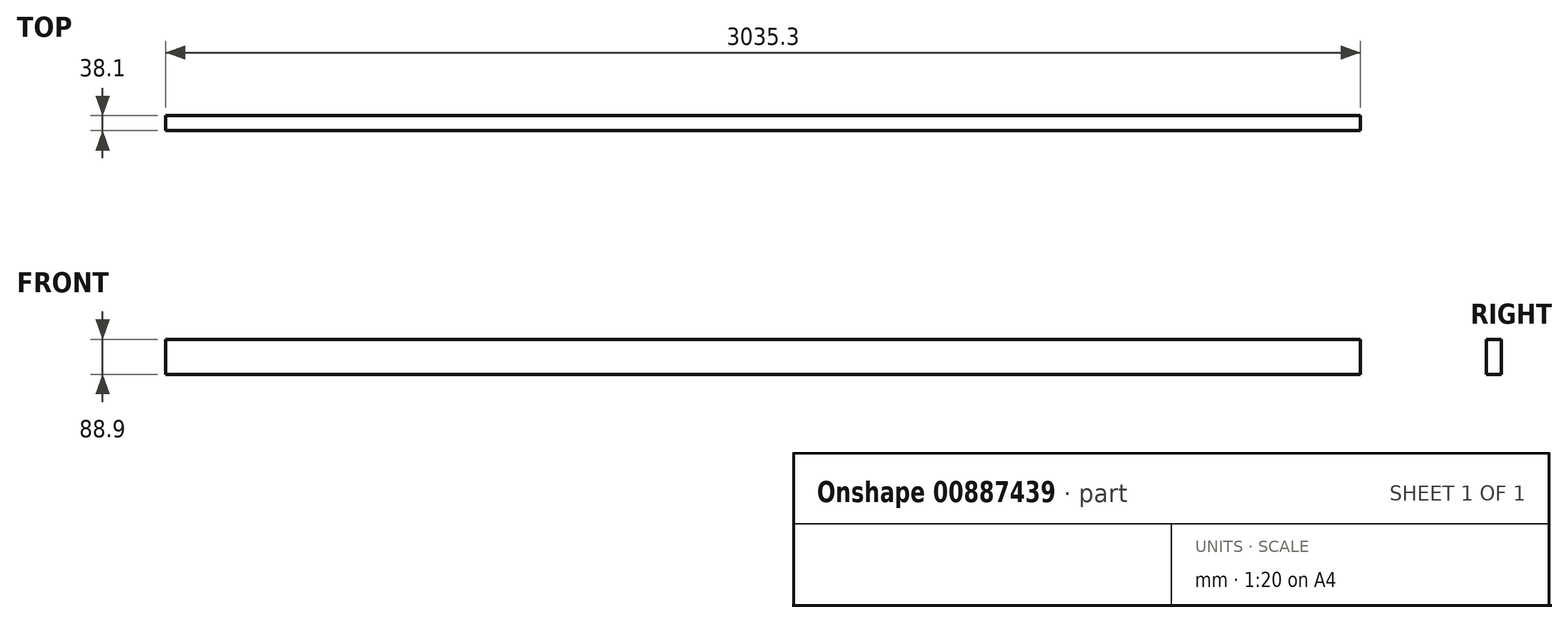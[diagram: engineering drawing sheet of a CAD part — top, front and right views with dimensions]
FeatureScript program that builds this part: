
annotation { "Feature Type Name" : "Feature", "Feature Type Description" : "" }
export const myFeature = defineFeature(function(context is Context, id is Id, definition is map)
    precondition{}
    {
        {
            var Q0;
            Q0=qCreatedBy(makeId("Top.planeOp"),FACE);
            var sketch = newSketch(context, id + "F0", { "sketchPlane" : qUnion([Q0])});
            skLineSegment(sketch, "E0.bottom", {"start": v(1517.65, 19.05) * mm, "end": v(-1517.65, 19.05) * mm});
            skLineSegment(sketch, "E0.top", {"start": v(1517.65, -19.05) * mm, "end": v(-1517.65, -19.05) * mm});
            skLineSegment(sketch, "E0.left", {"start": v(1517.65, 19.05) * mm, "end": v(1517.65, -19.05) * mm});
            skLineSegment(sketch, "E0.right", {"start": v(-1517.65, 19.05) * mm, "end": v(-1517.65, -19.05) * mm});
            skPoint(sketch, "E0.middle", {"position": v(0, 0) * mm});
            skSolve(sketch);
        }
        {
            var Q0;
            Q0=makeQuery(id+"F0.imprint","IMPRINT",FACE,{"disambiguationData":[TD([[makeQuery(id+"F0.imprint","IMPRINT",EDGE,{"derivedFrom":sQuery(id+"F0.wireOp",EDGE,"E0.bottom")}),1.0]])]});
            extrude(context, id + "F1", {"entities" : qUnion([Q0]), "depth" : 88.9 * mm, "offsetDistance" : 25.4 * mm});
        }
    });
